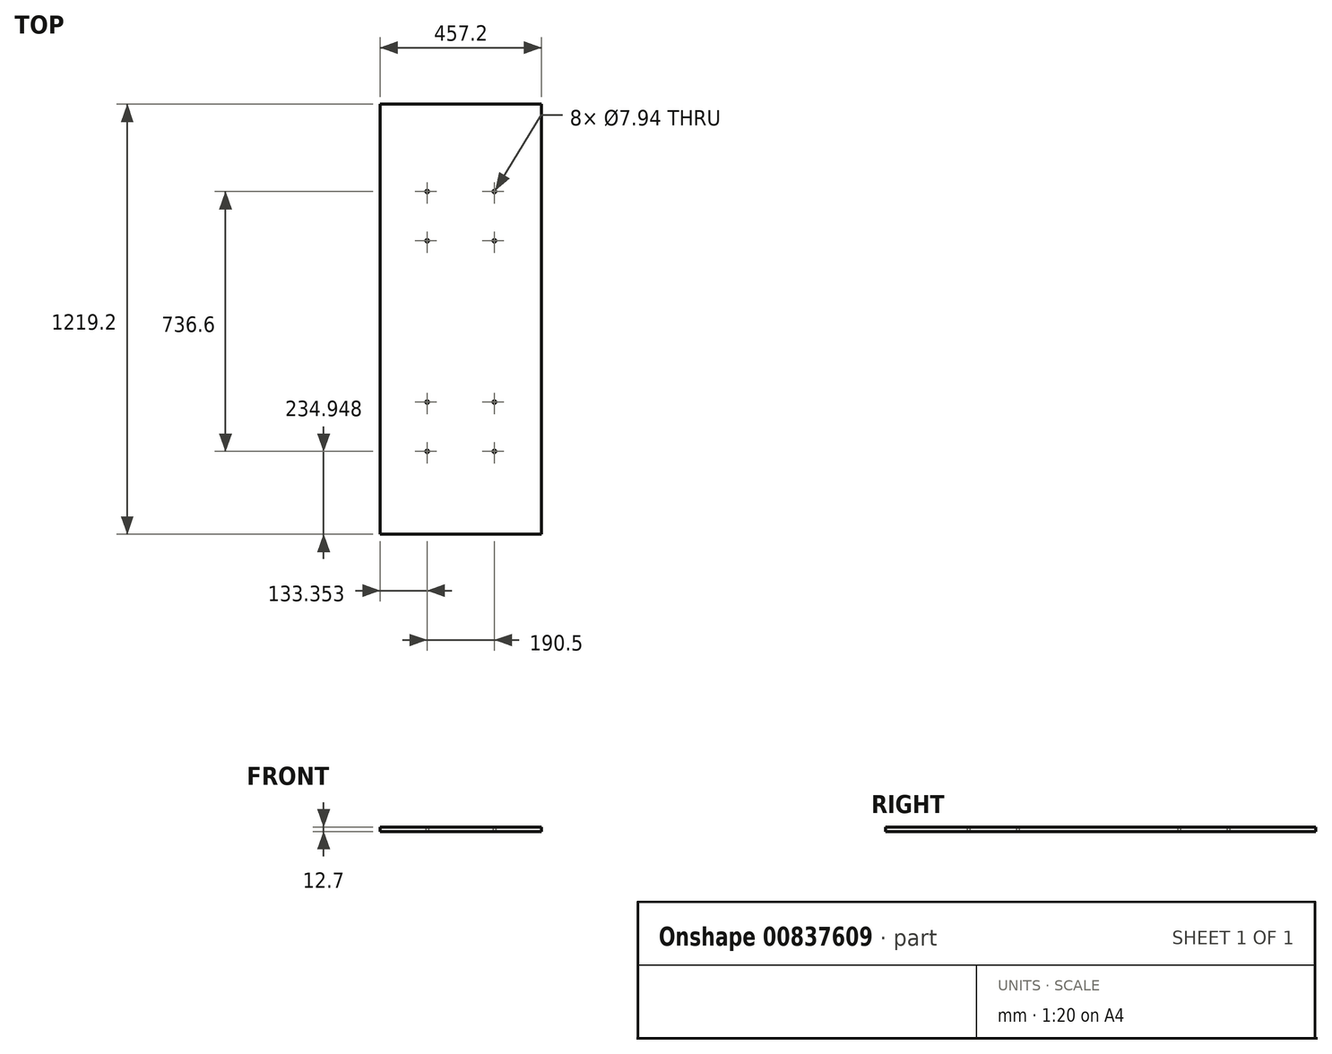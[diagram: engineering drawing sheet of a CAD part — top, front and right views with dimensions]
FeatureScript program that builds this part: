
annotation { "Feature Type Name" : "Feature", "Feature Type Description" : "" }
export const myFeature = defineFeature(function(context is Context, id is Id, definition is map)
    precondition{}
    {
        {
            var Q0;
            Q0=qCreatedBy(makeId("Top.planeOp"),FACE);
            var sketch = newSketch(context, id + "F0", { "sketchPlane" : qUnion([Q0])});
            skLineSegment(sketch, "E0.bottom", {"start": v(-274.12, -499.63) * mm, "end": v(-731.32, -499.63) * mm});
            skLineSegment(sketch, "E0.top", {"start": v(-274.12, 719.57) * mm, "end": v(-731.32, 719.57) * mm});
            skLineSegment(sketch, "E0.left", {"start": v(-274.12, -499.63) * mm, "end": v(-274.12, 719.57) * mm});
            skLineSegment(sketch, "E0.right", {"start": v(-731.32, -499.63) * mm, "end": v(-731.32, 719.57) * mm});
            skCircle(sketch, "E1", {"center": v(-597.97, 471.92) * mm, "radius": 3.97 * mm});
            skCircle(sketch, "E2", {"center": v(-407.47, 471.92) * mm, "radius": 3.97 * mm});
            skCircle(sketch, "E3", {"center": v(-597.97, 332.22) * mm, "radius": 3.97 * mm});
            skCircle(sketch, "E4", {"center": v(-407.47, 332.22) * mm, "radius": 3.97 * mm});
            skLineSegment(sketch, "E5", {"start": v(-731.32, 109.97) * mm, "end": v(-274.12, 109.97) * mm, "construction": true});
            skLineSegment(sketch, "E6", {"start": v(-502.72, 719.57) * mm, "end": v(-502.72, -499.63) * mm, "construction": true});
            skLineSegment(sketch, "E7", {"start": v(-597.97, 471.92) * mm, "end": v(-597.97, 332.22) * mm, "construction": true});
            skLineSegment(sketch, "E8", {"start": v(-407.47, 332.22) * mm, "end": v(-407.47, 471.92) * mm, "construction": true});
            skLineSegment(sketch, "E9", {"start": v(-407.47, 471.92) * mm, "end": v(-597.97, 471.92) * mm, "construction": true});
            skLineSegment(sketch, "E10", {"start": v(-597.97, 402.07) * mm, "end": v(-407.47, 402.07) * mm, "construction": true});
            skLineSegment(sketch, "E11", {"start": v(-502.72, 471.92) * mm, "end": v(-502.72, 402.07) * mm, "construction": true});
            skCircle(sketch, "E12", {"center": v(-597.97, -124.98) * mm, "radius": 3.97 * mm});
            skCircle(sketch, "E13", {"center": v(-407.47, -124.98) * mm, "radius": 3.97 * mm});
            skCircle(sketch, "E14", {"center": v(-597.97, -264.68) * mm, "radius": 3.97 * mm});
            skCircle(sketch, "E15", {"center": v(-407.47, -264.68) * mm, "radius": 3.97 * mm});
            skLineSegment(sketch, "E16", {"start": v(-597.97, -124.98) * mm, "end": v(-597.97, -264.68) * mm, "construction": true});
            skLineSegment(sketch, "E17", {"start": v(-407.47, -264.68) * mm, "end": v(-407.47, -124.98) * mm, "construction": true});
            skLineSegment(sketch, "E18", {"start": v(-407.47, -124.98) * mm, "end": v(-597.97, -124.98) * mm, "construction": true});
            skLineSegment(sketch, "E19", {"start": v(-597.97, -194.83) * mm, "end": v(-407.47, -194.83) * mm, "construction": true});
            skLineSegment(sketch, "E20", {"start": v(-502.72, -124.98) * mm, "end": v(-502.72, -194.83) * mm, "construction": true});
            skSolve(sketch);
        }
        {
            var Q0;
            Q0=makeQuery(id+"F0.imprint","IMPRINT",FACE,{"disambiguationData":[TD([[makeQuery(id+"F0.imprint","IMPRINT",EDGE,{"derivedFrom":sQuery(id+"F0.wireOp",EDGE,"E0.bottom")}),-1.0]])]});
            extrude(context, id + "F1", {"entities" : qUnion([Q0]), "depth" : 12.7 * mm, "offsetDistance" : 25.4 * mm});
        }
    });
